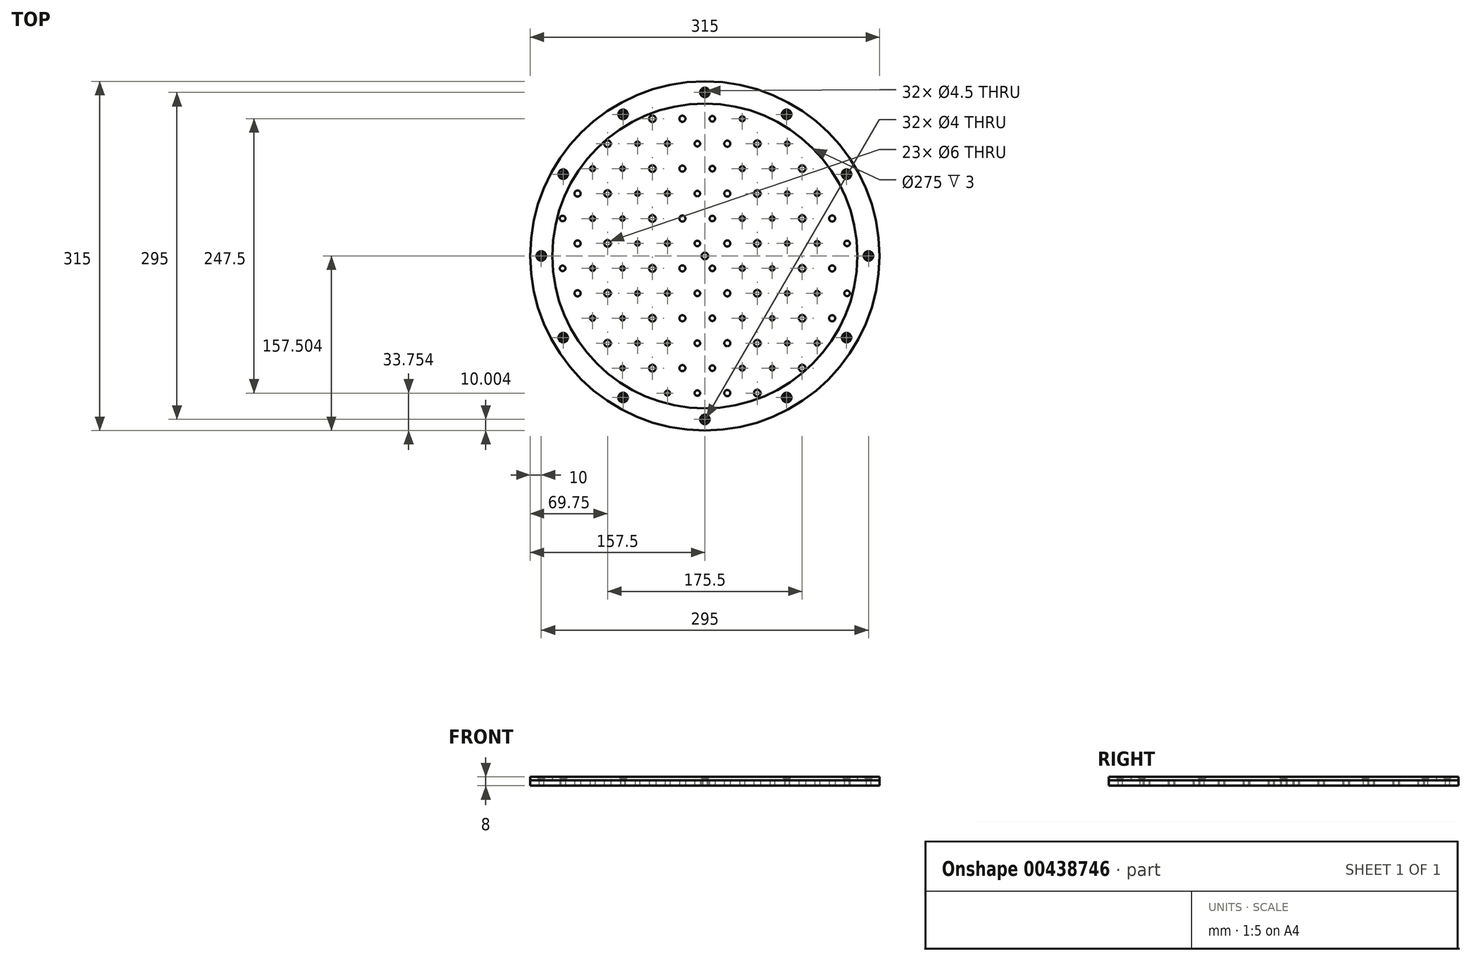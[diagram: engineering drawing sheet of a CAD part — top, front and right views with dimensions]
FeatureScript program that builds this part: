
annotation { "Feature Type Name" : "Feature", "Feature Type Description" : "" }
export const myFeature = defineFeature(function(context is Context, id is Id, definition is map)
    precondition{}
    {
        {
            var Q0;
            Q0=qCreatedBy(makeId("Top.planeOp"),FACE);
            var sketch = newSketch(context, id + "F0", { "sketchPlane" : qUnion([Q0])});
            skCircle(sketch, "E0", {"center": v(-81, 26.61) * mm, "radius": 2 * mm});
            skCircle(sketch, "E1", {"center": v(-54, 26.61) * mm, "radius": 2.25 * mm});
            skCircle(sketch, "E2", {"center": v(-27, 26.61) * mm, "radius": 2.5 * mm});
            skCircle(sketch, "E3", {"center": v(-67.5, 4.11) * mm, "radius": 3 * mm});
            skCircle(sketch, "E4", {"center": v(-40.5, 4.11) * mm, "radius": 2.75 * mm});
            skLineSegment(sketch, "E5", {"start": v(-87.75, 26.61) * mm, "end": v(47.25, 26.61) * mm, "construction": true});
            skLineSegment(sketch, "E6", {"start": v(-87.75, 4.11) * mm, "end": v(47.25, 4.11) * mm, "construction": true});
            skLineSegment(sketch, "E7.bottom", {"start": v(-87.75, 37.86) * mm, "end": v(47.25, 37.86) * mm});
            skLineSegment(sketch, "E7.top", {"start": v(-87.75, -7.14) * mm, "end": v(47.25, -7.14) * mm});
            skLineSegment(sketch, "E7.left", {"start": v(-87.75, 37.86) * mm, "end": v(-87.75, -7.14) * mm});
            skLineSegment(sketch, "E7.right", {"start": v(47.25, 37.86) * mm, "end": v(47.25, -7.14) * mm});
            skPoint(sketch, "E8.orphan", {"position": v(75.85, 26.61) * mm});
            skCircle(sketch, "E9", {"center": v(0, 26.61) * mm, "radius": 2.75 * mm});
            skCircle(sketch, "E10", {"center": v(27, 26.61) * mm, "radius": 3 * mm});
            skCircle(sketch, "E11", {"center": v(-13.5, 4.11) * mm, "radius": 2.5 * mm});
            skCircle(sketch, "E12", {"center": v(13.5, 4.11) * mm, "radius": 2.25 * mm});
            skCircle(sketch, "E13", {"center": v(40.5, 4.11) * mm, "radius": 2 * mm});
            skLineSegment(sketch, "E14", {"start": v(-20.25, 37.86) * mm, "end": v(-20.25, -7.14) * mm, "construction": true});
            skLineSegment(sketch, "E15", {"start": v(-87.75, 15.36) * mm, "end": v(47.25, 15.36) * mm, "construction": true});
            skPoint(sketch, "E16", {"position": v(-20.25, 15.36) * mm});
            skCircle(sketch, "E17.0.1.0", {"center": v(-67.5, 49.11) * mm, "radius": 3 * mm});
            skLineSegment(sketch, "E17.0.1.1", {"start": v(-87.75, 71.61) * mm, "end": v(47.25, 71.61) * mm, "construction": true});
            skLineSegment(sketch, "E17.0.1.2", {"start": v(-87.75, 49.11) * mm, "end": v(47.25, 49.11) * mm, "construction": true});
            skLineSegment(sketch, "E17.0.1.4", {"start": v(-87.75, 82.86) * mm, "end": v(47.25, 82.86) * mm});
            skLineSegment(sketch, "E17.0.1.6", {"start": v(-87.75, 82.86) * mm, "end": v(-87.75, 37.86) * mm});
            skLineSegment(sketch, "E17.0.1.7", {"start": v(47.25, 82.86) * mm, "end": v(47.25, 37.86) * mm});
            skLineSegment(sketch, "E17.0.1.8", {"start": v(-87.75, 60.36) * mm, "end": v(47.25, 60.36) * mm, "construction": true});
            skPoint(sketch, "E17.0.1.9", {"position": v(-20.25, 60.36) * mm});
            skPoint(sketch, "E17.0.1.10", {"position": v(75.85, 71.61) * mm});
            skLineSegment(sketch, "E17.0.1.11", {"start": v(-20.25, 82.86) * mm, "end": v(-20.25, 37.86) * mm, "construction": true});
            skCircle(sketch, "E17.0.1.12", {"center": v(-27, 71.61) * mm, "radius": 2.5 * mm});
            skCircle(sketch, "E17.0.1.13", {"center": v(-40.5, 49.11) * mm, "radius": 2.75 * mm});
            skCircle(sketch, "E17.0.1.14", {"center": v(-54, 71.61) * mm, "radius": 2.25 * mm});
            skCircle(sketch, "E17.0.1.15", {"center": v(-81, 71.61) * mm, "radius": 2 * mm});
            skCircle(sketch, "E17.0.1.16", {"center": v(40.5, 49.11) * mm, "radius": 2 * mm});
            skCircle(sketch, "E17.0.1.17", {"center": v(-13.5, 49.11) * mm, "radius": 2.5 * mm});
            skCircle(sketch, "E17.0.1.18", {"center": v(13.5, 49.11) * mm, "radius": 2.25 * mm});
            skCircle(sketch, "E17.0.1.19", {"center": v(0, 71.61) * mm, "radius": 2.75 * mm});
            skLineSegment(sketch, "E17.0.2.1", {"start": v(-87.75, 116.61) * mm, "end": v(47.25, 116.61) * mm, "construction": true});
            skLineSegment(sketch, "E17.0.2.2", {"start": v(-87.75, 94.11) * mm, "end": v(47.25, 94.11) * mm, "construction": true});
            skCircle(sketch, "E17.0.2.3", {"center": v(27, 116.61) * mm, "radius": 3 * mm});
            skLineSegment(sketch, "E17.0.2.5", {"start": v(-87.75, 82.86) * mm, "end": v(47.25, 82.86) * mm, "construction": true});
            skLineSegment(sketch, "E17.0.2.7", {"start": v(47.25, 127.86) * mm, "end": v(47.25, 82.86) * mm});
            skLineSegment(sketch, "E17.0.2.8", {"start": v(-87.75, 105.36) * mm, "end": v(47.25, 105.36) * mm, "construction": true});
            skPoint(sketch, "E17.0.2.9", {"position": v(-20.25, 105.36) * mm});
            skPoint(sketch, "E17.0.2.10", {"position": v(75.85, 116.61) * mm});
            skLineSegment(sketch, "E17.0.2.11", {"start": v(-20.25, 127.86) * mm, "end": v(-20.25, 82.86) * mm, "construction": true});
            skCircle(sketch, "E17.0.2.12", {"center": v(-27, 116.61) * mm, "radius": 2.5 * mm});
            skCircle(sketch, "E17.0.2.13", {"center": v(-40.5, 94.11) * mm, "radius": 2.75 * mm});
            skCircle(sketch, "E17.0.2.16", {"center": v(40.5, 94.11) * mm, "radius": 2 * mm});
            skCircle(sketch, "E17.0.2.17", {"center": v(-13.5, 94.11) * mm, "radius": 2.5 * mm});
            skCircle(sketch, "E17.0.2.18", {"center": v(13.5, 94.11) * mm, "radius": 2.25 * mm});
            skLineSegment(sketch, "E17.0.3.1", {"start": v(-87.75, 161.61) * mm, "end": v(47.25, 161.61) * mm, "construction": true});
            skLineSegment(sketch, "E17.0.3.2", {"start": v(-87.75, 139.11) * mm, "end": v(47.25, 139.11) * mm, "construction": true});
            skCircle(sketch, "E17.0.3.3", {"center": v(27, 161.61) * mm, "radius": 3 * mm});
            skLineSegment(sketch, "E17.0.3.7", {"start": v(47.25, 172.86) * mm, "end": v(47.25, 127.86) * mm});
            skLineSegment(sketch, "E17.0.3.8", {"start": v(-87.75, 150.36) * mm, "end": v(47.25, 150.36) * mm, "construction": true});
            skPoint(sketch, "E17.0.3.9", {"position": v(-20.25, 150.36) * mm});
            skPoint(sketch, "E17.0.3.10", {"position": v(75.85, 161.61) * mm});
            skLineSegment(sketch, "E17.0.3.11", {"start": v(-20.25, 172.86) * mm, "end": v(-20.25, 127.86) * mm, "construction": true});
            skCircle(sketch, "E17.0.3.12", {"center": v(-27, 161.61) * mm, "radius": 2.5 * mm});
            skCircle(sketch, "E17.0.3.13", {"center": v(-40.5, 139.11) * mm, "radius": 2.75 * mm});
            skCircle(sketch, "E17.0.3.16", {"center": v(40.5, 139.11) * mm, "radius": 2 * mm});
            skCircle(sketch, "E17.0.3.18", {"center": v(13.5, 139.11) * mm, "radius": 2.25 * mm});
            skCircle(sketch, "E17.0.3.19", {"center": v(0, 161.61) * mm, "radius": 2.75 * mm});
            skLineSegment(sketch, "E17.0.4.1", {"start": v(-87.75, 206.61) * mm, "end": v(47.25, 206.61) * mm, "construction": true});
            skLineSegment(sketch, "E17.0.4.2", {"start": v(-87.75, 184.11) * mm, "end": v(47.25, 184.11) * mm, "construction": true});
            skCircle(sketch, "E17.0.4.3", {"center": v(27, 206.61) * mm, "radius": 3 * mm});
            skLineSegment(sketch, "E17.0.4.7", {"start": v(47.25, 217.86) * mm, "end": v(47.25, 172.86) * mm});
            skLineSegment(sketch, "E17.0.4.8", {"start": v(-87.75, 195.36) * mm, "end": v(47.25, 195.36) * mm, "construction": true});
            skPoint(sketch, "E17.0.4.9", {"position": v(-20.25, 195.36) * mm});
            skPoint(sketch, "E17.0.4.10", {"position": v(75.85, 206.61) * mm});
            skLineSegment(sketch, "E17.0.4.11", {"start": v(-20.25, 217.86) * mm, "end": v(-20.25, 172.86) * mm, "construction": true});
            skCircle(sketch, "E17.0.4.12", {"center": v(-27, 206.61) * mm, "radius": 2.5 * mm});
            skCircle(sketch, "E17.0.4.13", {"center": v(-40.5, 184.11) * mm, "radius": 2.75 * mm});
            skCircle(sketch, "E17.0.4.16", {"center": v(40.5, 184.11) * mm, "radius": 2 * mm});
            skCircle(sketch, "E17.0.4.17", {"center": v(-13.5, 184.11) * mm, "radius": 2.5 * mm});
            skCircle(sketch, "E17.0.4.18", {"center": v(13.5, 184.11) * mm, "radius": 2.25 * mm});
            skCircle(sketch, "E17.0.4.19", {"center": v(0, 206.61) * mm, "radius": 2.75 * mm});
            skLineSegment(sketch, "E17.0.5.1", {"start": v(-87.75, 251.61) * mm, "end": v(47.25, 251.61) * mm, "construction": true});
            skLineSegment(sketch, "E17.0.5.2", {"start": v(-87.75, 229.11) * mm, "end": v(47.25, 229.11) * mm, "construction": true});
            skCircle(sketch, "E17.0.5.3", {"center": v(27, 251.61) * mm, "radius": 3 * mm});
            skLineSegment(sketch, "E17.0.5.7", {"start": v(47.25, 262.86) * mm, "end": v(47.25, 217.86) * mm});
            skLineSegment(sketch, "E17.0.5.8", {"start": v(-87.75, 240.36) * mm, "end": v(47.25, 240.36) * mm, "construction": true});
            skPoint(sketch, "E17.0.5.9", {"position": v(-20.25, 240.36) * mm});
            skPoint(sketch, "E17.0.5.10", {"position": v(75.85, 251.61) * mm});
            skLineSegment(sketch, "E17.0.5.11", {"start": v(-20.25, 262.86) * mm, "end": v(-20.25, 217.86) * mm, "construction": true});
            skCircle(sketch, "E17.0.5.13", {"center": v(-40.5, 229.11) * mm, "radius": 2.75 * mm});
            skCircle(sketch, "E17.0.5.16", {"center": v(40.5, 229.11) * mm, "radius": 2 * mm});
            skCircle(sketch, "E17.0.5.17", {"center": v(-13.5, 229.11) * mm, "radius": 2.5 * mm});
            skCircle(sketch, "E17.0.5.18", {"center": v(13.5, 229.11) * mm, "radius": 2.25 * mm});
            skCircle(sketch, "E17.0.5.19", {"center": v(0, 251.61) * mm, "radius": 2.75 * mm});
            skLineSegment(sketch, "E17.0.6.1", {"start": v(-87.75, 296.61) * mm, "end": v(47.25, 296.61) * mm, "construction": true});
            skLineSegment(sketch, "E17.0.6.2", {"start": v(-87.75, 274.11) * mm, "end": v(47.25, 274.11) * mm, "construction": true});
            skCircle(sketch, "E17.0.6.3", {"center": v(27, 296.61) * mm, "radius": 3 * mm});
            skLineSegment(sketch, "E17.0.6.8", {"start": v(-87.75, 285.36) * mm, "end": v(47.25, 285.36) * mm, "construction": true});
            skPoint(sketch, "E17.0.6.9", {"position": v(-20.25, 285.36) * mm});
            skPoint(sketch, "E17.0.6.10", {"position": v(75.85, 296.61) * mm});
            skLineSegment(sketch, "E17.0.6.11", {"start": v(-20.25, 307.86) * mm, "end": v(-20.25, 262.86) * mm, "construction": true});
            skCircle(sketch, "E17.0.6.12", {"center": v(-27, 296.61) * mm, "radius": 2.5 * mm});
            skCircle(sketch, "E17.0.6.13", {"center": v(-40.5, 274.11) * mm, "radius": 2.75 * mm});
            skCircle(sketch, "E17.0.6.16", {"center": v(40.5, 274.11) * mm, "radius": 2 * mm});
            skCircle(sketch, "E17.0.6.18", {"center": v(13.5, 274.11) * mm, "radius": 2.25 * mm});
            skLineSegment(sketch, "E17.0.7.1", {"start": v(-87.75, 341.61) * mm, "end": v(47.25, 341.61) * mm, "construction": true});
            skLineSegment(sketch, "E17.0.7.2", {"start": v(-87.75, 319.11) * mm, "end": v(47.25, 319.11) * mm, "construction": true});
            skCircle(sketch, "E17.0.7.3", {"center": v(27, 341.61) * mm, "radius": 3 * mm});
            skLineSegment(sketch, "E17.0.7.7", {"start": v(47.25, 352.86) * mm, "end": v(47.25, 307.86) * mm});
            skLineSegment(sketch, "E17.0.7.8", {"start": v(-87.75, 330.36) * mm, "end": v(47.25, 330.36) * mm, "construction": true});
            skPoint(sketch, "E17.0.7.9", {"position": v(-20.25, 330.36) * mm});
            skLineSegment(sketch, "E17.0.7.11", {"start": v(-20.25, 352.86) * mm, "end": v(-20.25, 307.86) * mm, "construction": true});
            skCircle(sketch, "E17.0.7.12", {"center": v(-27, 341.61) * mm, "radius": 2.5 * mm});
            skCircle(sketch, "E17.0.7.13", {"center": v(-40.5, 319.11) * mm, "radius": 2.75 * mm});
            skCircle(sketch, "E17.0.7.16", {"center": v(40.5, 319.11) * mm, "radius": 2 * mm});
            skCircle(sketch, "E17.0.7.17", {"center": v(-13.5, 319.11) * mm, "radius": 2.5 * mm});
            skCircle(sketch, "E17.0.7.18", {"center": v(13.5, 319.11) * mm, "radius": 2.25 * mm});
            skCircle(sketch, "E17.0.7.19", {"center": v(0, 341.61) * mm, "radius": 2.75 * mm});
            skCircle(sketch, "E17.1.0.0", {"center": v(67.5, 4.11) * mm, "radius": 3 * mm});
            skLineSegment(sketch, "E17.1.0.1", {"start": v(47.25, 26.61) * mm, "end": v(182.25, 26.61) * mm, "construction": true});
            skLineSegment(sketch, "E17.1.0.2", {"start": v(47.25, 4.11) * mm, "end": v(182.25, 4.11) * mm, "construction": true});
            skCircle(sketch, "E17.1.0.3", {"center": v(162, 26.61) * mm, "radius": 3 * mm});
            skLineSegment(sketch, "E17.1.0.4", {"start": v(47.25, 37.86) * mm, "end": v(182.25, 37.86) * mm});
            skLineSegment(sketch, "E17.1.0.5", {"start": v(47.25, -7.14) * mm, "end": v(182.25, -7.14) * mm});
            skLineSegment(sketch, "E17.1.0.7", {"start": v(182.25, 37.86) * mm, "end": v(182.25, -7.14) * mm});
            skLineSegment(sketch, "E17.1.0.8", {"start": v(47.25, 15.36) * mm, "end": v(182.25, 15.36) * mm, "construction": true});
            skPoint(sketch, "E17.1.0.9", {"position": v(114.75, 15.36) * mm});
            skPoint(sketch, "E17.1.0.10", {"position": v(210.85, 26.61) * mm});
            skLineSegment(sketch, "E17.1.0.11", {"start": v(114.75, 37.86) * mm, "end": v(114.75, -7.14) * mm, "construction": true});
            skCircle(sketch, "E17.1.0.12", {"center": v(108, 26.61) * mm, "radius": 2.5 * mm});
            skCircle(sketch, "E17.1.0.13", {"center": v(94.5, 4.11) * mm, "radius": 2.75 * mm});
            skCircle(sketch, "E17.1.0.14", {"center": v(81, 26.61) * mm, "radius": 2.25 * mm});
            skCircle(sketch, "E17.1.0.15", {"center": v(54, 26.61) * mm, "radius": 2 * mm});
            skCircle(sketch, "E17.1.0.16", {"center": v(175.5, 4.11) * mm, "radius": 2 * mm});
            skCircle(sketch, "E17.1.0.17", {"center": v(121.5, 4.11) * mm, "radius": 2.5 * mm});
            skCircle(sketch, "E17.1.0.18", {"center": v(148.5, 4.11) * mm, "radius": 2.25 * mm});
            skCircle(sketch, "E17.1.0.19", {"center": v(135, 26.61) * mm, "radius": 2.75 * mm});
            skCircle(sketch, "E17.1.1.0", {"center": v(67.5, 49.11) * mm, "radius": 3 * mm});
            skLineSegment(sketch, "E17.1.1.1", {"start": v(47.25, 71.61) * mm, "end": v(182.25, 71.61) * mm, "construction": true});
            skLineSegment(sketch, "E17.1.1.2", {"start": v(47.25, 49.11) * mm, "end": v(182.25, 49.11) * mm, "construction": true});
            skCircle(sketch, "E17.1.1.3", {"center": v(162, 71.61) * mm, "radius": 3 * mm});
            skLineSegment(sketch, "E17.1.1.5", {"start": v(47.25, 37.86) * mm, "end": v(182.25, 37.86) * mm});
            skLineSegment(sketch, "E17.1.1.6", {"start": v(47.25, 82.86) * mm, "end": v(47.25, 37.86) * mm});
            skLineSegment(sketch, "E17.1.1.7", {"start": v(182.25, 82.86) * mm, "end": v(182.25, 37.86) * mm});
            skLineSegment(sketch, "E17.1.1.8", {"start": v(47.25, 60.36) * mm, "end": v(182.25, 60.36) * mm, "construction": true});
            skPoint(sketch, "E17.1.1.9", {"position": v(114.75, 60.36) * mm});
            skPoint(sketch, "E17.1.1.10", {"position": v(210.85, 71.61) * mm});
            skLineSegment(sketch, "E17.1.1.11", {"start": v(114.75, 82.86) * mm, "end": v(114.75, 37.86) * mm, "construction": true});
            skCircle(sketch, "E17.1.1.12", {"center": v(108, 71.61) * mm, "radius": 2.5 * mm});
            skCircle(sketch, "E17.1.1.14", {"center": v(81, 71.61) * mm, "radius": 2.25 * mm});
            skCircle(sketch, "E17.1.1.16", {"center": v(175.5, 49.11) * mm, "radius": 2 * mm});
            skCircle(sketch, "E17.1.1.17", {"center": v(121.5, 49.11) * mm, "radius": 2.5 * mm});
            skCircle(sketch, "E17.1.1.19", {"center": v(135, 71.61) * mm, "radius": 2.75 * mm});
            skCircle(sketch, "E17.1.2.0", {"center": v(67.5, 94.11) * mm, "radius": 3 * mm});
            skLineSegment(sketch, "E17.1.2.1", {"start": v(47.25, 116.61) * mm, "end": v(182.25, 116.61) * mm, "construction": true});
            skLineSegment(sketch, "E17.1.2.2", {"start": v(47.25, 94.11) * mm, "end": v(182.25, 94.11) * mm, "construction": true});
            skCircle(sketch, "E17.1.2.3", {"center": v(162, 116.61) * mm, "radius": 3 * mm});
            skLineSegment(sketch, "E17.1.2.6", {"start": v(47.25, 127.86) * mm, "end": v(47.25, 82.86) * mm});
            skLineSegment(sketch, "E17.1.2.7", {"start": v(182.25, 127.86) * mm, "end": v(182.25, 82.86) * mm});
            skLineSegment(sketch, "E17.1.2.8", {"start": v(47.25, 105.36) * mm, "end": v(182.25, 105.36) * mm, "construction": true});
            skPoint(sketch, "E17.1.2.9", {"position": v(114.75, 105.36) * mm});
            skPoint(sketch, "E17.1.2.10", {"position": v(210.85, 116.61) * mm});
            skLineSegment(sketch, "E17.1.2.11", {"start": v(114.75, 127.86) * mm, "end": v(114.75, 82.86) * mm, "construction": true});
            skCircle(sketch, "E17.1.2.12", {"center": v(108, 116.61) * mm, "radius": 2.5 * mm});
            skCircle(sketch, "E17.1.2.13", {"center": v(94.5, 94.11) * mm, "radius": 2.75 * mm});
            skCircle(sketch, "E17.1.2.14", {"center": v(81, 116.61) * mm, "radius": 2.25 * mm});
            skCircle(sketch, "E17.1.2.15", {"center": v(54, 116.61) * mm, "radius": 2 * mm});
            skCircle(sketch, "E17.1.2.16", {"center": v(175.5, 94.11) * mm, "radius": 2 * mm});
            skCircle(sketch, "E17.1.2.17", {"center": v(121.5, 94.11) * mm, "radius": 2.5 * mm});
            skCircle(sketch, "E17.1.2.18", {"center": v(148.5, 94.11) * mm, "radius": 2.25 * mm});
            skCircle(sketch, "E17.1.2.19", {"center": v(135, 116.61) * mm, "radius": 2.75 * mm});
            skCircle(sketch, "E17.1.3.0", {"center": v(67.5, 139.11) * mm, "radius": 3 * mm});
            skLineSegment(sketch, "E17.1.3.1", {"start": v(47.25, 161.61) * mm, "end": v(182.25, 161.61) * mm, "construction": true});
            skLineSegment(sketch, "E17.1.3.2", {"start": v(47.25, 139.11) * mm, "end": v(182.25, 139.11) * mm, "construction": true});
            skCircle(sketch, "E17.1.3.3", {"center": v(162, 161.61) * mm, "radius": 3 * mm});
            skLineSegment(sketch, "E17.1.3.6", {"start": v(47.25, 172.86) * mm, "end": v(47.25, 127.86) * mm});
            skLineSegment(sketch, "E17.1.3.7", {"start": v(182.25, 172.86) * mm, "end": v(182.25, 127.86) * mm});
            skLineSegment(sketch, "E17.1.3.8", {"start": v(47.25, 150.36) * mm, "end": v(182.25, 150.36) * mm, "construction": true});
            skPoint(sketch, "E17.1.3.9", {"position": v(114.75, 150.36) * mm});
            skPoint(sketch, "E17.1.3.10", {"position": v(210.85, 161.61) * mm});
            skLineSegment(sketch, "E17.1.3.11", {"start": v(114.75, 172.86) * mm, "end": v(114.75, 127.86) * mm, "construction": true});
            skCircle(sketch, "E17.1.3.12", {"center": v(108, 161.61) * mm, "radius": 2.5 * mm});
            skCircle(sketch, "E17.1.3.13", {"center": v(94.5, 139.11) * mm, "radius": 2.75 * mm});
            skCircle(sketch, "E17.1.3.14", {"center": v(81, 161.61) * mm, "radius": 2.25 * mm});
            skCircle(sketch, "E17.1.3.15", {"center": v(54, 161.61) * mm, "radius": 2 * mm});
            skCircle(sketch, "E17.1.3.16", {"center": v(175.5, 139.11) * mm, "radius": 2 * mm});
            skCircle(sketch, "E17.1.3.17", {"center": v(121.5, 139.11) * mm, "radius": 2.5 * mm});
            skCircle(sketch, "E17.1.3.18", {"center": v(148.5, 139.11) * mm, "radius": 2.25 * mm});
            skCircle(sketch, "E17.1.3.19", {"center": v(135, 161.61) * mm, "radius": 2.75 * mm});
            skCircle(sketch, "E17.1.4.0", {"center": v(67.5, 184.11) * mm, "radius": 3 * mm});
            skLineSegment(sketch, "E17.1.4.1", {"start": v(47.25, 206.61) * mm, "end": v(182.25, 206.61) * mm, "construction": true});
            skLineSegment(sketch, "E17.1.4.2", {"start": v(47.25, 184.11) * mm, "end": v(182.25, 184.11) * mm, "construction": true});
            skCircle(sketch, "E17.1.4.3", {"center": v(162, 206.61) * mm, "radius": 3 * mm});
            skLineSegment(sketch, "E17.1.4.6", {"start": v(47.25, 217.86) * mm, "end": v(47.25, 172.86) * mm});
            skLineSegment(sketch, "E17.1.4.7", {"start": v(182.25, 217.86) * mm, "end": v(182.25, 172.86) * mm});
            skLineSegment(sketch, "E17.1.4.8", {"start": v(47.25, 195.36) * mm, "end": v(182.25, 195.36) * mm, "construction": true});
            skPoint(sketch, "E17.1.4.9", {"position": v(114.75, 195.36) * mm});
            skPoint(sketch, "E17.1.4.10", {"position": v(210.85, 206.61) * mm});
            skLineSegment(sketch, "E17.1.4.11", {"start": v(114.75, 217.86) * mm, "end": v(114.75, 172.86) * mm, "construction": true});
            skCircle(sketch, "E17.1.4.12", {"center": v(108, 206.61) * mm, "radius": 2.5 * mm});
            skCircle(sketch, "E17.1.4.13", {"center": v(94.5, 184.11) * mm, "radius": 2.75 * mm});
            skCircle(sketch, "E17.1.4.14", {"center": v(81, 206.61) * mm, "radius": 2.25 * mm});
            skCircle(sketch, "E17.1.4.15", {"center": v(54, 206.61) * mm, "radius": 2 * mm});
            skCircle(sketch, "E17.1.4.16", {"center": v(175.5, 184.11) * mm, "radius": 2 * mm});
            skCircle(sketch, "E17.1.4.17", {"center": v(121.5, 184.11) * mm, "radius": 2.5 * mm});
            skCircle(sketch, "E17.1.4.18", {"center": v(148.5, 184.11) * mm, "radius": 2.25 * mm});
            skCircle(sketch, "E17.1.4.19", {"center": v(135, 206.61) * mm, "radius": 2.75 * mm});
            skCircle(sketch, "E17.1.5.0", {"center": v(67.5, 229.11) * mm, "radius": 3 * mm});
            skLineSegment(sketch, "E17.1.5.1", {"start": v(47.25, 251.61) * mm, "end": v(182.25, 251.61) * mm, "construction": true});
            skLineSegment(sketch, "E17.1.5.2", {"start": v(47.25, 229.11) * mm, "end": v(182.25, 229.11) * mm, "construction": true});
            skCircle(sketch, "E17.1.5.3", {"center": v(162, 251.61) * mm, "radius": 3 * mm});
            skLineSegment(sketch, "E17.1.5.6", {"start": v(47.25, 262.86) * mm, "end": v(47.25, 217.86) * mm});
            skLineSegment(sketch, "E17.1.5.7", {"start": v(182.25, 262.86) * mm, "end": v(182.25, 217.86) * mm});
            skLineSegment(sketch, "E17.1.5.8", {"start": v(47.25, 240.36) * mm, "end": v(182.25, 240.36) * mm, "construction": true});
            skPoint(sketch, "E17.1.5.9", {"position": v(114.75, 240.36) * mm});
            skPoint(sketch, "E17.1.5.10", {"position": v(210.85, 251.61) * mm});
            skLineSegment(sketch, "E17.1.5.11", {"start": v(114.75, 262.86) * mm, "end": v(114.75, 217.86) * mm, "construction": true});
            skCircle(sketch, "E17.1.5.12", {"center": v(108, 251.61) * mm, "radius": 2.5 * mm});
            skCircle(sketch, "E17.1.5.13", {"center": v(94.5, 229.11) * mm, "radius": 2.75 * mm});
            skCircle(sketch, "E17.1.5.14", {"center": v(81, 251.61) * mm, "radius": 2.25 * mm});
            skCircle(sketch, "E17.1.5.15", {"center": v(54, 251.61) * mm, "radius": 2 * mm});
            skCircle(sketch, "E17.1.5.16", {"center": v(175.5, 229.11) * mm, "radius": 2 * mm});
            skCircle(sketch, "E17.1.5.17", {"center": v(121.5, 229.11) * mm, "radius": 2.5 * mm});
            skCircle(sketch, "E17.1.5.18", {"center": v(148.5, 229.11) * mm, "radius": 2.25 * mm});
            skCircle(sketch, "E17.1.5.19", {"center": v(135, 251.61) * mm, "radius": 2.75 * mm});
            skCircle(sketch, "E17.1.6.0", {"center": v(67.5, 274.11) * mm, "radius": 3 * mm});
            skLineSegment(sketch, "E17.1.6.1", {"start": v(47.25, 296.61) * mm, "end": v(182.25, 296.61) * mm, "construction": true});
            skLineSegment(sketch, "E17.1.6.2", {"start": v(47.25, 274.11) * mm, "end": v(182.25, 274.11) * mm, "construction": true});
            skCircle(sketch, "E17.1.6.3", {"center": v(162, 296.61) * mm, "radius": 3 * mm});
            skLineSegment(sketch, "E17.1.6.8", {"start": v(47.25, 285.36) * mm, "end": v(182.25, 285.36) * mm, "construction": true});
            skPoint(sketch, "E17.1.6.9", {"position": v(114.75, 285.36) * mm});
            skPoint(sketch, "E17.1.6.10", {"position": v(210.85, 296.61) * mm});
            skLineSegment(sketch, "E17.1.6.11", {"start": v(114.75, 307.86) * mm, "end": v(114.75, 262.86) * mm, "construction": true});
            skCircle(sketch, "E17.1.6.12", {"center": v(108, 296.61) * mm, "radius": 2.5 * mm});
            skCircle(sketch, "E17.1.6.13", {"center": v(94.5, 274.11) * mm, "radius": 2.75 * mm});
            skCircle(sketch, "E17.1.6.14", {"center": v(81, 296.61) * mm, "radius": 2.25 * mm});
            skCircle(sketch, "E17.1.6.15", {"center": v(54, 296.61) * mm, "radius": 2 * mm});
            skCircle(sketch, "E17.1.6.16", {"center": v(175.5, 274.11) * mm, "radius": 2 * mm});
            skCircle(sketch, "E17.1.6.17", {"center": v(121.5, 274.11) * mm, "radius": 2.5 * mm});
            skCircle(sketch, "E17.1.6.18", {"center": v(148.5, 274.11) * mm, "radius": 2.25 * mm});
            skCircle(sketch, "E17.1.6.19", {"center": v(135, 296.61) * mm, "radius": 2.75 * mm});
            skCircle(sketch, "E17.1.7.0", {"center": v(67.5, 319.11) * mm, "radius": 3 * mm});
            skLineSegment(sketch, "E17.1.7.1", {"start": v(47.25, 341.61) * mm, "end": v(182.25, 341.61) * mm, "construction": true});
            skLineSegment(sketch, "E17.1.7.2", {"start": v(47.25, 319.11) * mm, "end": v(182.25, 319.11) * mm, "construction": true});
            skLineSegment(sketch, "E17.1.7.6", {"start": v(47.25, 352.86) * mm, "end": v(47.25, 307.86) * mm});
            skLineSegment(sketch, "E17.1.7.7", {"start": v(182.25, 352.86) * mm, "end": v(182.25, 307.86) * mm});
            skLineSegment(sketch, "E17.1.7.8", {"start": v(47.25, 330.36) * mm, "end": v(182.25, 330.36) * mm, "construction": true});
            skPoint(sketch, "E17.1.7.9", {"position": v(114.75, 330.36) * mm});
            skLineSegment(sketch, "E17.1.7.11", {"start": v(114.75, 352.86) * mm, "end": v(114.75, 307.86) * mm, "construction": true});
            skCircle(sketch, "E17.1.7.12", {"center": v(108, 341.61) * mm, "radius": 2.5 * mm});
            skCircle(sketch, "E17.1.7.13", {"center": v(94.5, 319.11) * mm, "radius": 2.75 * mm});
            skCircle(sketch, "E17.1.7.15", {"center": v(54, 341.61) * mm, "radius": 2 * mm});
            skCircle(sketch, "E17.1.7.17", {"center": v(121.5, 319.11) * mm, "radius": 2.5 * mm});
            skCircle(sketch, "E17.1.7.18", {"center": v(148.5, 319.11) * mm, "radius": 2.25 * mm});
            skCircle(sketch, "E17.2.0.0", {"center": v(202.5, 4.11) * mm, "radius": 3 * mm});
            skLineSegment(sketch, "E17.2.0.6", {"start": v(182.25, 37.86) * mm, "end": v(182.25, -7.14) * mm});
            skPoint(sketch, "E17.2.0.9", {"position": v(249.75, 15.36) * mm});
            skLineSegment(sketch, "E17.2.0.11", {"start": v(249.75, 37.86) * mm, "end": v(249.75, -7.14) * mm, "construction": true});
            skCircle(sketch, "E17.2.0.12", {"center": v(243, 26.61) * mm, "radius": 2.5 * mm});
            skCircle(sketch, "E17.2.0.13", {"center": v(229.5, 4.11) * mm, "radius": 2.75 * mm});
            skCircle(sketch, "E17.2.0.14", {"center": v(216, 26.61) * mm, "radius": 2.25 * mm});
            skCircle(sketch, "E17.2.0.15", {"center": v(189, 26.61) * mm, "radius": 2 * mm});
            skCircle(sketch, "E17.2.0.17", {"center": v(256.5, 4.11) * mm, "radius": 2.5 * mm});
            skCircle(sketch, "E17.2.1.0", {"center": v(202.5, 49.11) * mm, "radius": 3 * mm});
            skLineSegment(sketch, "E17.2.1.6", {"start": v(182.25, 82.86) * mm, "end": v(182.25, 37.86) * mm});
            skPoint(sketch, "E17.2.1.9", {"position": v(249.75, 60.36) * mm});
            skLineSegment(sketch, "E17.2.1.11", {"start": v(249.75, 82.86) * mm, "end": v(249.75, 37.86) * mm, "construction": true});
            skCircle(sketch, "E17.2.1.12", {"center": v(243, 71.61) * mm, "radius": 2.5 * mm});
            skCircle(sketch, "E17.2.1.13", {"center": v(229.5, 49.11) * mm, "radius": 2.75 * mm});
            skCircle(sketch, "E17.2.1.14", {"center": v(216, 71.61) * mm, "radius": 2.25 * mm});
            skCircle(sketch, "E17.2.1.15", {"center": v(189, 71.61) * mm, "radius": 2 * mm});
            skCircle(sketch, "E17.2.1.17", {"center": v(256.5, 49.11) * mm, "radius": 2.5 * mm});
            skCircle(sketch, "E17.2.2.0", {"center": v(202.5, 94.11) * mm, "radius": 3 * mm});
            skLineSegment(sketch, "E17.2.2.6", {"start": v(182.25, 127.86) * mm, "end": v(182.25, 82.86) * mm});
            skPoint(sketch, "E17.2.2.9", {"position": v(249.75, 105.36) * mm});
            skLineSegment(sketch, "E17.2.2.11", {"start": v(249.75, 127.86) * mm, "end": v(249.75, 82.86) * mm, "construction": true});
            skCircle(sketch, "E17.2.2.14", {"center": v(216, 116.61) * mm, "radius": 2.25 * mm});
            skCircle(sketch, "E17.2.2.15", {"center": v(189, 116.61) * mm, "radius": 2 * mm});
            skCircle(sketch, "E17.2.2.17", {"center": v(256.5, 94.11) * mm, "radius": 2.5 * mm});
            skCircle(sketch, "E17.2.3.0", {"center": v(202.5, 139.11) * mm, "radius": 3 * mm});
            skLineSegment(sketch, "E17.2.3.6", {"start": v(182.25, 172.86) * mm, "end": v(182.25, 127.86) * mm});
            skPoint(sketch, "E17.2.3.9", {"position": v(249.75, 150.36) * mm});
            skLineSegment(sketch, "E17.2.3.11", {"start": v(249.75, 172.86) * mm, "end": v(249.75, 127.86) * mm, "construction": true});
            skCircle(sketch, "E17.2.3.12", {"center": v(243, 161.61) * mm, "radius": 2.5 * mm});
            skCircle(sketch, "E17.2.3.13", {"center": v(229.5, 139.11) * mm, "radius": 2.75 * mm});
            skCircle(sketch, "E17.2.3.14", {"center": v(216, 161.61) * mm, "radius": 2.25 * mm});
            skCircle(sketch, "E17.2.3.15", {"center": v(189, 161.61) * mm, "radius": 2 * mm});
            skCircle(sketch, "E17.2.4.0", {"center": v(202.5, 184.11) * mm, "radius": 3 * mm});
            skLineSegment(sketch, "E17.2.4.6", {"start": v(182.25, 217.86) * mm, "end": v(182.25, 172.86) * mm});
            skPoint(sketch, "E17.2.4.9", {"position": v(249.75, 195.36) * mm});
            skLineSegment(sketch, "E17.2.4.11", {"start": v(249.75, 217.86) * mm, "end": v(249.75, 172.86) * mm, "construction": true});
            skCircle(sketch, "E17.2.4.12", {"center": v(243, 206.61) * mm, "radius": 2.5 * mm});
            skCircle(sketch, "E17.2.4.13", {"center": v(229.5, 184.11) * mm, "radius": 2.75 * mm});
            skCircle(sketch, "E17.2.4.14", {"center": v(216, 206.61) * mm, "radius": 2.25 * mm});
            skCircle(sketch, "E17.2.4.15", {"center": v(189, 206.61) * mm, "radius": 2 * mm});
            skCircle(sketch, "E17.2.4.17", {"center": v(256.5, 184.11) * mm, "radius": 2.5 * mm});
            skCircle(sketch, "E17.2.5.0", {"center": v(202.5, 229.11) * mm, "radius": 3 * mm});
            skLineSegment(sketch, "E17.2.5.6", {"start": v(182.25, 262.86) * mm, "end": v(182.25, 217.86) * mm});
            skPoint(sketch, "E17.2.5.9", {"position": v(249.75, 240.36) * mm});
            skLineSegment(sketch, "E17.2.5.11", {"start": v(249.75, 262.86) * mm, "end": v(249.75, 217.86) * mm, "construction": true});
            skCircle(sketch, "E17.2.5.13", {"center": v(229.5, 229.11) * mm, "radius": 2.75 * mm});
            skCircle(sketch, "E17.2.5.14", {"center": v(216, 251.61) * mm, "radius": 2.25 * mm});
            skCircle(sketch, "E17.2.5.15", {"center": v(189, 251.61) * mm, "radius": 2 * mm});
            skCircle(sketch, "E17.2.5.17", {"center": v(256.5, 229.11) * mm, "radius": 2.5 * mm});
            skCircle(sketch, "E17.2.6.0", {"center": v(202.5, 274.11) * mm, "radius": 3 * mm});
            skPoint(sketch, "E17.2.6.9", {"position": v(249.75, 285.36) * mm});
            skLineSegment(sketch, "E17.2.6.11", {"start": v(249.75, 307.86) * mm, "end": v(249.75, 262.86) * mm, "construction": true});
            skCircle(sketch, "E17.2.6.12", {"center": v(243, 296.61) * mm, "radius": 2.5 * mm});
            skCircle(sketch, "E17.2.6.14", {"center": v(216, 296.61) * mm, "radius": 2.25 * mm});
            skCircle(sketch, "E17.2.6.15", {"center": v(189, 296.61) * mm, "radius": 2 * mm});
            skCircle(sketch, "E17.2.6.17", {"center": v(256.5, 274.11) * mm, "radius": 2.5 * mm});
            skLineSegment(sketch, "E17.2.7.6", {"start": v(182.25, 352.86) * mm, "end": v(182.25, 307.86) * mm, "construction": true});
            skPoint(sketch, "E17.2.7.9", {"position": v(249.75, 330.36) * mm});
            skLineSegment(sketch, "E17.2.7.11", {"start": v(249.75, 352.86) * mm, "end": v(249.75, 307.86) * mm, "construction": true});
            skCircle(sketch, "E17.2.7.12", {"center": v(243, 341.61) * mm, "radius": 2.5 * mm});
            skCircle(sketch, "E17.2.7.13", {"center": v(229.5, 319.11) * mm, "radius": 2.75 * mm});
            skCircle(sketch, "E17.2.7.14", {"center": v(216, 341.61) * mm, "radius": 2.25 * mm});
            skCircle(sketch, "E17.2.7.15", {"center": v(189, 341.61) * mm, "radius": 2 * mm});
            skCircle(sketch, "E17.2.7.17", {"center": v(256.5, 319.11) * mm, "radius": 2.5 * mm});
            skLineSegment(sketch, "E17.direction1", {"start": v(-87.75, -7.14) * mm, "end": v(47.25, -7.14) * mm, "construction": true});
            skLineSegment(sketch, "E17.direction2", {"start": v(-87.75, -7.14) * mm, "end": v(-87.75, 37.86) * mm, "construction": true});
            skCircle(sketch, "E18", {"center": v(114.75, 195.36) * mm, "radius": 137.5 * mm});
            skCircle(sketch, "E19", {"center": v(114.82, 195.34) * mm, "radius": 3 * mm});
            skSolve(sketch);
        }
        {
            var Q0;
            Q0=makeQuery(id+"F0.imprint","IMPRINT",FACE,{"disambiguationData":[TD([[makeQuery(id+"F0.imprint","IMPRINT",EDGE,{"derivedFrom":sQuery(id+"F0.wireOp",EDGE,"E17.1.7.0")}),-1.0]])]});
            var Q1;
            Q1=makeQuery(id+"F0.imprint","IMPRINT",FACE,{"disambiguationData":[TD([[makeQuery(id+"F0.imprint","IMPRINT",EDGE,{"derivedFrom":sQuery(id+"F0.wireOp",EDGE,"E17.1.6.0")}),-1.0]])]});
            var Q2;
            Q2=makeQuery(id+"F0.imprint","IMPRINT",FACE,{"disambiguationData":[TD([[makeQuery(id+"F0.imprint","IMPRINT",EDGE,{"derivedFrom":sQuery(id+"F0.wireOp",EDGE,"E17.0.7.16")}),-1.0]])]});
            var Q3;
            Q3=makeQuery(id+"F0.imprint","IMPRINT",FACE,{"disambiguationData":[TD([[makeQuery(id+"F0.imprint","IMPRINT",EDGE,{"derivedFrom":sQuery(id+"F0.wireOp",EDGE,"E17.2.6.0")}),-1.0]])]});
            var Q4;
            Q4=makeQuery(id+"F0.imprint","IMPRINT",FACE,{"disambiguationData":[TD([[makeQuery(id+"F0.imprint","IMPRINT",EDGE,{"derivedFrom":sQuery(id+"F0.wireOp",EDGE,"E17.0.6.3")}),-1.0]])]});
            var Q5;
            Q5=makeQuery(id+"F0.imprint","IMPRINT",FACE,{"disambiguationData":[TD([[makeQuery(id+"F0.imprint","IMPRINT",EDGE,{"derivedFrom":sQuery(id+"F0.wireOp",EDGE,"E17.0.5.3")}),-1.0]])]});
            var Q6;
            Q6=makeQuery(id+"F0.imprint","IMPRINT",FACE,{"disambiguationData":[TD([[makeQuery(id+"F0.imprint","IMPRINT",EDGE,{"derivedFrom":sQuery(id+"F0.wireOp",EDGE,"E17.1.5.0")}),-1.0]])]});
            var Q7;
            Q7=makeQuery(id+"F0.imprint","IMPRINT",FACE,{"disambiguationData":[TD([[makeQuery(id+"F0.imprint","IMPRINT",EDGE,{"derivedFrom":sQuery(id+"F0.wireOp",EDGE,"E17.2.5.0")}),-1.0]])]});
            var Q8;
            Q8=makeQuery(id+"F0.imprint","IMPRINT",FACE,{"disambiguationData":[TD([[makeQuery(id+"F0.imprint","IMPRINT",EDGE,{"derivedFrom":sQuery(id+"F0.wireOp",EDGE,"E17.0.4.3")}),-1.0]])]});
            var Q9;
            Q9=makeQuery(id+"F0.imprint","IMPRINT",FACE,{"disambiguationData":[TD([[makeQuery(id+"F0.imprint","IMPRINT",EDGE,{"derivedFrom":sQuery(id+"F0.wireOp",EDGE,"E17.1.4.0")}),-1.0]])]});
            var Q10;
            Q10=makeQuery(id+"F0.imprint","IMPRINT",FACE,{"disambiguationData":[TD([[makeQuery(id+"F0.imprint","IMPRINT",EDGE,{"derivedFrom":sQuery(id+"F0.wireOp",EDGE,"E17.2.4.0")}),-1.0]])]});
            var Q11;
            {var subQ3=sQuery(id+"F0.wireOp",EDGE,"E18");var subQ6=sQuery(id+"F0.wireOp",EDGE,"E17.2.7.0");var subQ8=makeQuery(id+"F0.imprint","INTERSECT",VERTEX,{"disambiguationData":[OD(0.0)],"derivedFrom":[subQ6,subQ3]});Q11=makeQuery(id+"F0.imprint","IMPRINT",FACE,{"disambiguationData":[TD([[makeQuery(id+"F0.imprint","IMPRINT",EDGE,{"disambiguationData":[TD([[subQ8,1.0]])],"derivedFrom":subQ6}),-1.0]])]});}
            var Q12;
            Q12=makeQuery(id+"F0.imprint","IMPRINT",FACE,{"disambiguationData":[TD([[makeQuery(id+"F0.imprint","IMPRINT",EDGE,{"derivedFrom":sQuery(id+"F0.wireOp",EDGE,"E17.0.3.3")}),-1.0]])]});
            var Q13;
            Q13=makeQuery(id+"F0.imprint","IMPRINT",FACE,{"disambiguationData":[TD([[makeQuery(id+"F0.imprint","IMPRINT",EDGE,{"derivedFrom":sQuery(id+"F0.wireOp",EDGE,"E17.1.3.0")}),-1.0]])]});
            var Q14;
            Q14=makeQuery(id+"F0.imprint","IMPRINT",FACE,{"disambiguationData":[TD([[makeQuery(id+"F0.imprint","IMPRINT",EDGE,{"derivedFrom":sQuery(id+"F0.wireOp",EDGE,"E17.2.3.0")}),-1.0]])]});
            var Q15;
            Q15=makeQuery(id+"F0.imprint","IMPRINT",FACE,{"disambiguationData":[TD([[makeQuery(id+"F0.imprint","IMPRINT",EDGE,{"derivedFrom":sQuery(id+"F0.wireOp",EDGE,"E17.0.2.3")}),-1.0]])]});
            var Q16;
            Q16=makeQuery(id+"F0.imprint","IMPRINT",FACE,{"disambiguationData":[TD([[makeQuery(id+"F0.imprint","IMPRINT",EDGE,{"derivedFrom":sQuery(id+"F0.wireOp",EDGE,"E17.1.2.0")}),-1.0]])]});
            var Q17;
            Q17=makeQuery(id+"F0.imprint","IMPRINT",FACE,{"disambiguationData":[TD([[makeQuery(id+"F0.imprint","IMPRINT",EDGE,{"derivedFrom":sQuery(id+"F0.wireOp",EDGE,"E17.2.2.0")}),-1.0]])]});
            var Q18;
            Q18=makeQuery(id+"F0.imprint","IMPRINT",FACE,{"disambiguationData":[TD([[makeQuery(id+"F0.imprint","IMPRINT",EDGE,{"derivedFrom":sQuery(id+"F0.wireOp",EDGE,"E17.1.1.3")}),-1.0]])]});
            var Q19;
            Q19=makeQuery(id+"F0.imprint","IMPRINT",FACE,{"disambiguationData":[TD([[makeQuery(id+"F0.imprint","IMPRINT",EDGE,{"derivedFrom":sQuery(id+"F0.wireOp",EDGE,"E17.2.1.15")}),-1.0]])]});
            var Q20;
            {var subQ0=sQuery(id+"F0.wireOp",EDGE,"E18");var subQ1=sQuery(id+"F0.wireOp",EDGE,"E17.0.1.3");var subQ2=makeQuery(id+"F0.imprint","INTERSECT",VERTEX,{"disambiguationData":[OD(0.0)],"derivedFrom":[subQ1,subQ0]});Q20=makeQuery(id+"F0.imprint","IMPRINT",FACE,{"disambiguationData":[TD([[makeQuery(id+"F0.imprint","IMPRINT",EDGE,{"disambiguationData":[TD([[subQ2,1.0]])],"derivedFrom":subQ1}),-1.0]])]});}
            var Q21;
            {var subQ1=sQuery(id+"F0.wireOp",EDGE,"E17.0.1.4");var subQ3=sQuery(id+"F0.wireOp",EDGE,"E18");var subQ4=makeQuery(id+"F0.imprint","INTERSECT",VERTEX,{"derivedFrom":[subQ1,subQ3]});Q21=makeQuery(id+"F0.imprint","IMPRINT",FACE,{"disambiguationData":[TD([[makeQuery(id+"F0.imprint","IMPRINT",EDGE,{"disambiguationData":[TD([[subQ4,-1.0]])],"derivedFrom":subQ3}),1.0]])]});}
            extrude(context, id + "F1", {"entities" : qUnion([Q0, Q1, Q2, Q3, Q4, Q5, Q6, Q7, Q8, Q9, Q10, Q11, Q12, Q13, Q14, Q15, Q16, Q17, Q18, Q19, Q20, Q21]), "depth" : 5 * mm});
        }
        {
            var Q0;
            Q0=qCreatedBy(makeId("Top.planeOp"),FACE);
            var sketch = newSketch(context, id + "F2", { "sketchPlane" : qUnion([Q0])});
            skCircle(sketch, "E20.0", {"center": v(114.75, 195.36) * mm, "radius": 137.5 * mm});
            skCircle(sketch, "E21", {"center": v(114.75, 195.36) * mm, "radius": 157.5 * mm});
            skLineSegment(sketch, "E22", {"start": v(114.75, 352.86) * mm, "end": v(114.75, 37.86) * mm, "construction": true});
            skCircle(sketch, "E23", {"center": v(114.75, 195.36) * mm, "radius": 147.5 * mm, "construction": true});
            skCircle(sketch, "E24", {"center": v(114.75, 342.86) * mm, "radius": 2 * mm});
            skCircle(sketch, "E25.1.0", {"center": v(41, 323.1) * mm, "radius": 2 * mm});
            skCircle(sketch, "E25.2.0", {"center": v(-12.99, 269.11) * mm, "radius": 2 * mm});
            skCircle(sketch, "E25.3.0", {"center": v(-32.75, 195.36) * mm, "radius": 2 * mm});
            skCircle(sketch, "E25.4.0", {"center": v(-12.99, 121.61) * mm, "radius": 2 * mm});
            skCircle(sketch, "E25.5.0", {"center": v(41, 67.63) * mm, "radius": 2 * mm});
            skCircle(sketch, "E25.6.0", {"center": v(114.75, 47.86) * mm, "radius": 2 * mm});
            skCircle(sketch, "E25.7.0", {"center": v(188.5, 67.63) * mm, "radius": 2 * mm});
            skCircle(sketch, "E25.8.0", {"center": v(242.49, 121.61) * mm, "radius": 2 * mm});
            skCircle(sketch, "E25.9.0", {"center": v(262.25, 195.36) * mm, "radius": 2 * mm});
            skCircle(sketch, "E25.10.0", {"center": v(242.49, 269.11) * mm, "radius": 2 * mm});
            skCircle(sketch, "E25.11.0", {"center": v(188.5, 323.1) * mm, "radius": 2 * mm});
            skSolve(sketch);
        }
        {
            var Q0;
            Q0=makeQuery(id+"F2.imprint","IMPRINT",FACE,{"disambiguationData":[TD([[makeQuery(id+"F2.imprint","IMPRINT",EDGE,{"derivedFrom":sQuery(id+"F2.wireOp",EDGE,"E20.0")}),-1.0]])]});
            extrude(context, id + "F3", {"entities" : qUnion([Q0]), "operationType" : NewBodyOperationType.ADD, "depth" : 5 * mm});
        }
        {
            var Q0;
            Q0=makeQuery(id+"F3.boolean.opBoolean","MERGE",FACE,{"derivedFrom":[makeQuery(id+"F1.opExtrude","CAP_FACE",FACE,{"disambiguationData":[OSD([sQuery(id+"F0.wireOp",EDGE,"E17.0.2.3"),sQuery(id+"F0.wireOp",EDGE,"E17.0.2.16"),sQuery(id+"F0.wireOp",EDGE,"E17.0.3.3"),sQuery(id+"F0.wireOp",EDGE,"E17.0.3.16"),sQuery(id+"F0.wireOp",EDGE,"E17.0.3.18"),sQuery(id+"F0.wireOp",EDGE,"E17.0.3.19"),sQuery(id+"F0.wireOp",EDGE,"E17.0.4.3"),sQuery(id+"F0.wireOp",EDGE,"E17.0.4.16"),sQuery(id+"F0.wireOp",EDGE,"E17.0.4.17"),sQuery(id+"F0.wireOp",EDGE,"E17.0.4.18"),sQuery(id+"F0.wireOp",EDGE,"E17.0.4.19"),sQuery(id+"F0.wireOp",EDGE,"E17.0.5.3"),sQuery(id+"F0.wireOp",EDGE,"E17.0.5.16"),sQuery(id+"F0.wireOp",EDGE,"E17.0.5.17"),sQuery(id+"F0.wireOp",EDGE,"E17.0.5.18"),sQuery(id+"F0.wireOp",EDGE,"E17.0.5.19"),sQuery(id+"F0.wireOp",EDGE,"E17.0.6.3"),sQuery(id+"F0.wireOp",EDGE,"E17.0.6.16"),sQuery(id+"F0.wireOp",EDGE,"E17.0.6.18"),sQuery(id+"F0.wireOp",EDGE,"E17.1.1.3"),sQuery(id+"F0.wireOp",EDGE,"E17.1.1.12"),sQuery(id+"F0.wireOp",EDGE,"E17.1.1.14"),sQuery(id+"F0.wireOp",EDGE,"E17.1.1.19"),sQuery(id+"F0.wireOp",EDGE,"E17.1.2.0"),sQuery(id+"F0.wireOp",EDGE,"E17.1.2.3"),sQuery(id+"F0.wireOp",EDGE,"E17.1.2.12"),sQuery(id+"F0.wireOp",EDGE,"E17.1.2.13"),sQuery(id+"F0.wireOp",EDGE,"E17.1.2.14"),sQuery(id+"F0.wireOp",EDGE,"E17.1.2.15"),sQuery(id+"F0.wireOp",EDGE,"E17.1.2.16"),sQuery(id+"F0.wireOp",EDGE,"E17.1.2.17"),sQuery(id+"F0.wireOp",EDGE,"E17.1.2.18"),sQuery(id+"F0.wireOp",EDGE,"E17.1.2.19"),sQuery(id+"F0.wireOp",EDGE,"E17.1.3.0"),sQuery(id+"F0.wireOp",EDGE,"E17.1.3.3"),sQuery(id+"F0.wireOp",EDGE,"E17.1.3.12"),sQuery(id+"F0.wireOp",EDGE,"E17.1.3.13"),sQuery(id+"F0.wireOp",EDGE,"E17.1.3.14"),sQuery(id+"F0.wireOp",EDGE,"E17.1.3.15"),sQuery(id+"F0.wireOp",EDGE,"E17.1.3.16"),sQuery(id+"F0.wireOp",EDGE,"E17.1.3.17"),sQuery(id+"F0.wireOp",EDGE,"E17.1.3.18"),sQuery(id+"F0.wireOp",EDGE,"E17.1.3.19"),sQuery(id+"F0.wireOp",EDGE,"E17.1.4.0"),sQuery(id+"F0.wireOp",EDGE,"E17.1.4.3"),sQuery(id+"F0.wireOp",EDGE,"E17.1.4.12"),sQuery(id+"F0.wireOp",EDGE,"E17.1.4.13"),sQuery(id+"F0.wireOp",EDGE,"E17.1.4.14"),sQuery(id+"F0.wireOp",EDGE,"E17.1.4.15"),sQuery(id+"F0.wireOp",EDGE,"E17.1.4.16"),sQuery(id+"F0.wireOp",EDGE,"E17.1.4.17"),sQuery(id+"F0.wireOp",EDGE,"E17.1.4.18"),sQuery(id+"F0.wireOp",EDGE,"E17.1.4.19"),sQuery(id+"F0.wireOp",EDGE,"E17.1.5.0"),sQuery(id+"F0.wireOp",EDGE,"E17.1.5.3"),sQuery(id+"F0.wireOp",EDGE,"E17.1.5.12"),sQuery(id+"F0.wireOp",EDGE,"E17.1.5.13"),sQuery(id+"F0.wireOp",EDGE,"E17.1.5.14"),sQuery(id+"F0.wireOp",EDGE,"E17.1.5.15"),sQuery(id+"F0.wireOp",EDGE,"E17.1.5.16"),sQuery(id+"F0.wireOp",EDGE,"E17.1.5.17"),sQuery(id+"F0.wireOp",EDGE,"E17.1.5.18"),sQuery(id+"F0.wireOp",EDGE,"E17.1.5.19"),sQuery(id+"F0.wireOp",EDGE,"E17.1.6.0"),sQuery(id+"F0.wireOp",EDGE,"E17.1.6.3"),sQuery(id+"F0.wireOp",EDGE,"E17.1.6.12"),sQuery(id+"F0.wireOp",EDGE,"E17.1.6.13"),sQuery(id+"F0.wireOp",EDGE,"E17.1.6.14"),sQuery(id+"F0.wireOp",EDGE,"E17.1.6.15"),sQuery(id+"F0.wireOp",EDGE,"E17.1.6.16"),sQuery(id+"F0.wireOp",EDGE,"E17.1.6.17"),sQuery(id+"F0.wireOp",EDGE,"E17.1.6.18"),sQuery(id+"F0.wireOp",EDGE,"E17.1.6.19"),sQuery(id+"F0.wireOp",EDGE,"E17.1.7.0"),sQuery(id+"F0.wireOp",EDGE,"E17.1.7.13"),sQuery(id+"F0.wireOp",EDGE,"E17.1.7.17"),sQuery(id+"F0.wireOp",EDGE,"E17.1.7.18"),sQuery(id+"F0.wireOp",EDGE,"E17.2.2.0"),sQuery(id+"F0.wireOp",EDGE,"E17.2.2.14"),sQuery(id+"F0.wireOp",EDGE,"E17.2.2.15"),sQuery(id+"F0.wireOp",EDGE,"E17.2.3.0"),sQuery(id+"F0.wireOp",EDGE,"E17.2.3.12"),sQuery(id+"F0.wireOp",EDGE,"E17.2.3.13"),sQuery(id+"F0.wireOp",EDGE,"E17.2.3.14"),sQuery(id+"F0.wireOp",EDGE,"E17.2.3.15"),sQuery(id+"F0.wireOp",EDGE,"E17.2.4.0"),sQuery(id+"F0.wireOp",EDGE,"E17.2.4.12"),sQuery(id+"F0.wireOp",EDGE,"E17.2.4.13"),sQuery(id+"F0.wireOp",EDGE,"E17.2.4.14"),sQuery(id+"F0.wireOp",EDGE,"E17.2.4.15"),sQuery(id+"F0.wireOp",EDGE,"E17.2.5.0"),sQuery(id+"F0.wireOp",EDGE,"E17.2.5.13"),sQuery(id+"F0.wireOp",EDGE,"E17.2.5.14"),sQuery(id+"F0.wireOp",EDGE,"E17.2.5.15"),sQuery(id+"F0.wireOp",EDGE,"E17.2.6.0"),sQuery(id+"F0.wireOp",EDGE,"E17.2.6.15"),sQuery(id+"F0.wireOp",EDGE,"E18")])],"isStart":false}),makeQuery(id+"F3.opExtrude","CAP_FACE",FACE,{"disambiguationData":[OSD([sQuery(id+"F2.wireOp",EDGE,"E20.0"),sQuery(id+"F2.wireOp",EDGE,"E21"),sQuery(id+"F2.wireOp",EDGE,"E24"),sQuery(id+"F2.wireOp",EDGE,"E25.1.0"),sQuery(id+"F2.wireOp",EDGE,"E25.2.0"),sQuery(id+"F2.wireOp",EDGE,"E25.3.0"),sQuery(id+"F2.wireOp",EDGE,"E25.4.0"),sQuery(id+"F2.wireOp",EDGE,"E25.5.0"),sQuery(id+"F2.wireOp",EDGE,"E25.6.0"),sQuery(id+"F2.wireOp",EDGE,"E25.7.0"),sQuery(id+"F2.wireOp",EDGE,"E25.8.0"),sQuery(id+"F2.wireOp",EDGE,"E25.9.0"),sQuery(id+"F2.wireOp",EDGE,"E25.10.0"),sQuery(id+"F2.wireOp",EDGE,"E25.11.0")])],"isStart":false})]});
            var sketch = newSketch(context, id + "F4", { "sketchPlane" : qUnion([Q0])});
            skCircle(sketch, "E26.0", {"center": v(114.75, 195.36) * mm, "radius": 157.5 * mm});
            skCircle(sketch, "E27", {"center": v(114.75, 195.36) * mm, "radius": 137.5 * mm});
            skCircle(sketch, "E28.0", {"center": v(114.75, 342.86) * mm, "radius": 2 * mm});
            skCircle(sketch, "E29.0", {"center": v(188.5, 323.1) * mm, "radius": 2 * mm});
            skCircle(sketch, "E30.0", {"center": v(242.49, 269.11) * mm, "radius": 2 * mm});
            skCircle(sketch, "E31.0", {"center": v(262.25, 195.36) * mm, "radius": 2 * mm});
            skCircle(sketch, "E32.0", {"center": v(242.49, 121.61) * mm, "radius": 2 * mm});
            skCircle(sketch, "E33.0", {"center": v(188.5, 67.63) * mm, "radius": 2 * mm});
            skCircle(sketch, "E34.0", {"center": v(114.75, 47.86) * mm, "radius": 2 * mm});
            skCircle(sketch, "E35.0", {"center": v(41, 67.63) * mm, "radius": 2 * mm});
            skCircle(sketch, "E36.0", {"center": v(-12.99, 121.61) * mm, "radius": 2 * mm});
            skCircle(sketch, "E37.0", {"center": v(-32.75, 195.36) * mm, "radius": 2 * mm});
            skCircle(sketch, "E38.0", {"center": v(-12.99, 269.11) * mm, "radius": 2 * mm});
            skCircle(sketch, "E39.0", {"center": v(41, 323.1) * mm, "radius": 2 * mm});
            skCircle(sketch, "E40", {"center": v(114.75, 342.86) * mm, "radius": 2.25 * mm});
            skCircle(sketch, "E41.1.0", {"center": v(41, 323.1) * mm, "radius": 2.25 * mm});
            skCircle(sketch, "E41.2.0", {"center": v(-12.99, 269.11) * mm, "radius": 2.25 * mm});
            skCircle(sketch, "E41.3.0", {"center": v(-32.75, 195.36) * mm, "radius": 2.25 * mm});
            skCircle(sketch, "E41.4.0", {"center": v(-12.99, 121.61) * mm, "radius": 2.25 * mm});
            skCircle(sketch, "E41.5.0", {"center": v(41, 67.63) * mm, "radius": 2.25 * mm});
            skCircle(sketch, "E41.6.0", {"center": v(114.75, 47.86) * mm, "radius": 2.25 * mm});
            skCircle(sketch, "E41.7.0", {"center": v(188.5, 67.63) * mm, "radius": 2.25 * mm});
            skCircle(sketch, "E41.8.0", {"center": v(242.49, 121.61) * mm, "radius": 2.25 * mm});
            skCircle(sketch, "E41.9.0", {"center": v(262.25, 195.36) * mm, "radius": 2.25 * mm});
            skCircle(sketch, "E41.10.0", {"center": v(242.49, 269.11) * mm, "radius": 2.25 * mm});
            skCircle(sketch, "E41.11.0", {"center": v(188.5, 323.1) * mm, "radius": 2.25 * mm});
            skSolve(sketch);
        }
        {
            var Q0;
            Q0=makeQuery(id+"F4.imprint","IMPRINT",FACE,{"disambiguationData":[TD([[makeQuery(id+"F4.imprint","IMPRINT",EDGE,{"derivedFrom":sQuery(id+"F4.wireOp",EDGE,"E26.0")}),1.0]])]});
            extrude(context, id + "F5", {"entities" : qUnion([Q0]), "depth" : 3 * mm});
        }
        {
            var Q0;
            Q0=makeQuery(id+"F5.opExtrude","CAP_EDGE",EDGE,{"disambiguationData":[OSD([sQuery(id+"F4.wireOp",EDGE,"E40")])],"isStart":false});
            var Q1;
            Q1=makeQuery(id+"F5.opExtrude","CAP_EDGE",EDGE,{"disambiguationData":[OSD([sQuery(id+"F4.wireOp",EDGE,"E41.11.0")])],"isStart":false});
            var Q2;
            Q2=makeQuery(id+"F5.opExtrude","CAP_EDGE",EDGE,{"disambiguationData":[OSD([sQuery(id+"F4.wireOp",EDGE,"E41.10.0")])],"isStart":false});
            var Q3;
            Q3=makeQuery(id+"F5.opExtrude","CAP_EDGE",EDGE,{"disambiguationData":[OSD([sQuery(id+"F4.wireOp",EDGE,"E41.9.0")])],"isStart":false});
            var Q4;
            Q4=makeQuery(id+"F5.opExtrude","CAP_EDGE",EDGE,{"disambiguationData":[OSD([sQuery(id+"F4.wireOp",EDGE,"E41.8.0")])],"isStart":false});
            var Q5;
            Q5=makeQuery(id+"F5.opExtrude","CAP_EDGE",EDGE,{"disambiguationData":[OSD([sQuery(id+"F4.wireOp",EDGE,"E41.1.0")])],"isStart":false});
            var Q6;
            Q6=makeQuery(id+"F5.opExtrude","CAP_EDGE",EDGE,{"disambiguationData":[OSD([sQuery(id+"F4.wireOp",EDGE,"E41.2.0")])],"isStart":false});
            var Q7;
            Q7=makeQuery(id+"F5.opExtrude","CAP_EDGE",EDGE,{"disambiguationData":[OSD([sQuery(id+"F4.wireOp",EDGE,"E41.3.0")])],"isStart":false});
            var Q8;
            Q8=makeQuery(id+"F5.opExtrude","CAP_EDGE",EDGE,{"disambiguationData":[OSD([sQuery(id+"F4.wireOp",EDGE,"E41.4.0")])],"isStart":false});
            var Q9;
            Q9=makeQuery(id+"F5.opExtrude","CAP_EDGE",EDGE,{"disambiguationData":[OSD([sQuery(id+"F4.wireOp",EDGE,"E41.5.0")])],"isStart":false});
            var Q10;
            Q10=makeQuery(id+"F5.opExtrude","CAP_EDGE",EDGE,{"disambiguationData":[OSD([sQuery(id+"F4.wireOp",EDGE,"E41.6.0")])],"isStart":false});
            var Q11;
            Q11=makeQuery(id+"F5.opExtrude","CAP_EDGE",EDGE,{"disambiguationData":[OSD([sQuery(id+"F4.wireOp",EDGE,"E41.7.0")])],"isStart":false});
            chamfer(context, id + "F6", {"entities" : qUnion([Q0, Q1, Q2, Q3, Q4, Q5, Q6, Q7, Q8, Q9, Q10, Q11]), "width" : 2 * mm, "tangentPropagation" : true});
        }
    });
